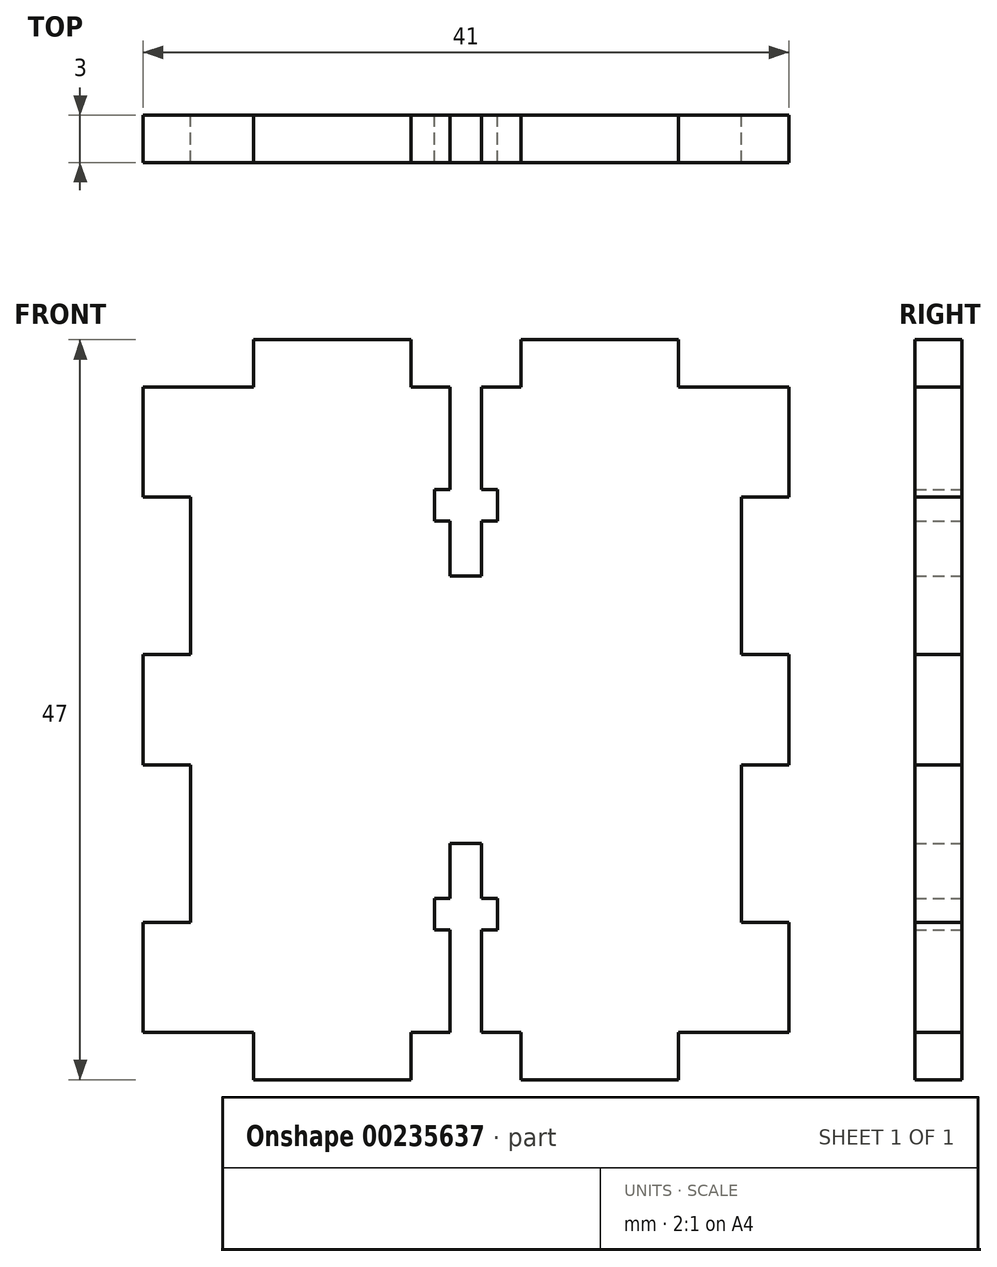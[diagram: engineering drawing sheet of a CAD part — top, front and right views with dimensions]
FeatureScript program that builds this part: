
annotation { "Feature Type Name" : "Feature", "Feature Type Description" : "" }
export const myFeature = defineFeature(function(context is Context, id is Id, definition is map)
    precondition{}
    {
        {
            var Q0;
            Q0=qCreatedBy(makeId("Front.planeOp"),FACE);
            var sketch = newSketch(context, id + "F0", { "sketchPlane" : qUnion([Q0])});
            skLineSegment(sketch, "E0", {"start": v(3, 0) * mm, "end": v(0, 0) * mm});
            skLineSegment(sketch, "E1", {"start": v(3, 0) * mm, "end": v(3, 7) * mm});
            skLineSegment(sketch, "E2", {"start": v(3, 7) * mm, "end": v(0, 7) * mm});
            skLineSegment(sketch, "E3", {"start": v(0, 7) * mm, "end": v(0, 17) * mm});
            skLineSegment(sketch, "E4", {"start": v(0, 17) * mm, "end": v(3, 17) * mm});
            skLineSegment(sketch, "E5", {"start": v(3, 17) * mm, "end": v(3, 24) * mm});
            skLineSegment(sketch, "E6", {"start": v(3, 24) * mm, "end": v(0, 24) * mm});
            skLineSegment(sketch, "E7", {"start": v(0, 24) * mm, "end": v(0, 34) * mm});
            skLineSegment(sketch, "E8", {"start": v(0, 34) * mm, "end": v(3, 34) * mm});
            skLineSegment(sketch, "E9", {"start": v(3, 34) * mm, "end": v(3, 41) * mm});
            skLineSegment(sketch, "E10", {"start": v(3, 41) * mm, "end": v(-4, 41) * mm});
            skLineSegment(sketch, "E11", {"start": v(-4, 41) * mm, "end": v(-4, 44) * mm});
            skLineSegment(sketch, "E12", {"start": v(-4, 44) * mm, "end": v(-14, 44) * mm});
            skLineSegment(sketch, "E13", {"start": v(-14, 44) * mm, "end": v(-14, 41) * mm});
            skLineSegment(sketch, "E14", {"start": v(-14, 41) * mm, "end": v(-16.5, 41) * mm});
            skLineSegment(sketch, "E15", {"start": v(-21, 41) * mm, "end": v(-21, 44) * mm});
            skLineSegment(sketch, "E16", {"start": v(-31, 44) * mm, "end": v(-31, 41) * mm});
            skLineSegment(sketch, "E17", {"start": v(-31, 41) * mm, "end": v(-38, 41) * mm});
            skLineSegment(sketch, "E18", {"start": v(-38, 41) * mm, "end": v(-38, 34) * mm});
            skLineSegment(sketch, "E19", {"start": v(-38, 34) * mm, "end": v(-35, 34) * mm});
            skLineSegment(sketch, "E20", {"start": v(-35, 24) * mm, "end": v(-35, 34) * mm});
            skLineSegment(sketch, "E21", {"start": v(-35, 24) * mm, "end": v(-38, 24) * mm});
            skLineSegment(sketch, "E22", {"start": v(-31, 44) * mm, "end": v(-21, 44) * mm});
            skLineSegment(sketch, "E23", {"start": v(-38, 24) * mm, "end": v(-38, 17) * mm});
            skLineSegment(sketch, "E24", {"start": v(-38, 17) * mm, "end": v(-35, 17) * mm});
            skLineSegment(sketch, "E25", {"start": v(-35, 17) * mm, "end": v(-35, 7) * mm});
            skLineSegment(sketch, "E26", {"start": v(-35, 7) * mm, "end": v(-38, 7) * mm});
            skLineSegment(sketch, "E27", {"start": v(-38, 7) * mm, "end": v(-38, 0) * mm});
            skLineSegment(sketch, "E28", {"start": v(-38, 0) * mm, "end": v(-31, 0) * mm});
            skLineSegment(sketch, "E29", {"start": v(-31, 0) * mm, "end": v(-31, -3) * mm});
            skLineSegment(sketch, "E30", {"start": v(-31, -3) * mm, "end": v(-31, 0) * mm});
            skLineSegment(sketch, "E31", {"start": v(-31, -3) * mm, "end": v(-21, -3) * mm});
            skLineSegment(sketch, "E32", {"start": v(-21, -3) * mm, "end": v(-21, 0) * mm});
            skLineSegment(sketch, "E33", {"start": v(-21, 0) * mm, "end": v(-18.5, 0) * mm});
            skLineSegment(sketch, "E34", {"start": v(-14, 0) * mm, "end": v(-14, -3) * mm});
            skLineSegment(sketch, "E35", {"start": v(-14, -3) * mm, "end": v(-4, -3) * mm});
            skLineSegment(sketch, "E36", {"start": v(-4, -3) * mm, "end": v(-4, 0) * mm});
            skLineSegment(sketch, "E37", {"start": v(-4, 0) * mm, "end": v(3, 0) * mm});
            skLineSegment(sketch, "E38", {"start": v(-17.5, 41) * mm, "end": v(-17.5, 18.94) * mm, "construction": true});
            skLineSegment(sketch, "E39.top", {"start": v(-18.5, 29) * mm, "end": v(-16.5, 29) * mm});
            skLineSegment(sketch, "E39.left", {"start": v(-18.5, 41) * mm, "end": v(-18.5, 34.5) * mm});
            skLineSegment(sketch, "E39.right", {"start": v(-16.5, 41) * mm, "end": v(-16.5, 34.5) * mm});
            skLineSegment(sketch, "E40", {"start": v(-21, 41) * mm, "end": v(-18.5, 41) * mm});
            skLineSegment(sketch, "E41.bottom", {"start": v(-19.5, 34.5) * mm, "end": v(-18.5, 34.5) * mm});
            skLineSegment(sketch, "E41.top", {"start": v(-19.5, 32.5) * mm, "end": v(-18.5, 32.5) * mm});
            skLineSegment(sketch, "E41.left", {"start": v(-19.5, 34.5) * mm, "end": v(-19.5, 32.5) * mm});
            skLineSegment(sketch, "E41.right", {"start": v(-15.5, 34.5) * mm, "end": v(-15.5, 32.5) * mm});
            skLineSegment(sketch, "E42.trimOffspring", {"start": v(-16.5, 34.5) * mm, "end": v(-15.5, 34.5) * mm});
            skLineSegment(sketch, "E43.trimOffspring", {"start": v(-16.5, 32.5) * mm, "end": v(-16.5, 29) * mm});
            skLineSegment(sketch, "E44.trimOffspring", {"start": v(-16.5, 32.5) * mm, "end": v(-15.5, 32.5) * mm});
            skLineSegment(sketch, "E45.trimOffspring", {"start": v(-18.5, 32.5) * mm, "end": v(-18.5, 29) * mm});
            skPoint(sketch, "E46.orphan", {"position": v(-38, 20.5) * mm});
            skLineSegment(sketch, "E47.MirrorCS", {"start": v(-16.5, 8.5) * mm, "end": v(-15.5, 8.5) * mm});
            skLineSegment(sketch, "E48.MirrorCS", {"start": v(-19.5, 8.5) * mm, "end": v(-18.5, 8.5) * mm});
            skLineSegment(sketch, "E49.MirrorCS", {"start": v(-16.5, 6.5) * mm, "end": v(-15.5, 6.5) * mm});
            skLineSegment(sketch, "E50.MirrorCS", {"start": v(-19.5, 6.5) * mm, "end": v(-18.5, 6.5) * mm});
            skLineSegment(sketch, "E51.MirrorCS", {"start": v(-16.5, 8.5) * mm, "end": v(-16.5, 12) * mm});
            skLineSegment(sketch, "E52.MirrorCS", {"start": v(-18.5, 0) * mm, "end": v(-18.5, 6.5) * mm});
            skLineSegment(sketch, "E53.MirrorCS", {"start": v(-18.5, 12) * mm, "end": v(-16.5, 12) * mm});
            skLineSegment(sketch, "E54.MirrorCS", {"start": v(-15.5, 6.5) * mm, "end": v(-15.5, 8.5) * mm});
            skLineSegment(sketch, "E55.MirrorCS", {"start": v(-18.5, 8.5) * mm, "end": v(-18.5, 12) * mm});
            skLineSegment(sketch, "E56.MirrorCS", {"start": v(-16.5, 0) * mm, "end": v(-16.5, 6.5) * mm});
            skLineSegment(sketch, "E57.MirrorCS", {"start": v(-19.5, 6.5) * mm, "end": v(-19.5, 8.5) * mm});
            skLineSegment(sketch, "E58.MirrorCS", {"start": v(-14, 0) * mm, "end": v(-16.5, 0) * mm});
            skLineSegment(sketch, "E59.trimOffspring", {"start": v(-16.5, 0) * mm, "end": v(-14, 0) * mm});
            skSolve(sketch);
        }
        {
            var Q0;
            Q0 = qSketchRegion(id + "F0", true);
            extrude(context, id + "F1", {"entities" : qUnion([Q0]), "depth" : 3 * mm});
        }
    });
